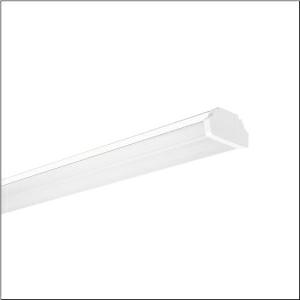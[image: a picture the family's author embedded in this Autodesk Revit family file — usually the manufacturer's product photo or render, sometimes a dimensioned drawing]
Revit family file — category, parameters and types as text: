
# Revit family: dus_31_gen_2_53bd812dv4a5c23sl3_ab9d
name_source: partatom
category: Lighting Fixtures
units: mm (PartAtom-declared; Revit-internal decimal feet)

## family parameters
Cut with Voids When Loaded = No
Host = Face
Light Source = No
Part Type = Normal
Room Calculation Point = No
Round Connector Dimension = Use Diameter
Shared = No

## types (1)
- --- (1 x LED, 950 lm, 6.3 W, 4000K)
    Apparent Load = 6 VA
    CIE Flux Codes = 47 80 95 93 100
    Color Rendering = 80
    Color Temperature = 4000K
    Default Elevation = 1800 mm
    Description = DUS 31 Gen.2, luminaire insert, of sheet steel, coil coated, white, length: 1.535mm, width: 81mm, height: 90mm, 5x system unit, system units: 307mm, LED rated luminous flux: 10.860lm, light colour: 840, SDCM (Standard Deviation of Colour Matching)MacAdam ≤ 3 SDCM (initial), control gear: DALI 2, with plug, 6-pole, with phase selection (L1, L2), mains connection: 220..240V, AC, 50/60Hz, rated input power: 65W, for emergency light function, charging phase on L3 (wire number 3), through-wiring accessed according to module size, converter,control gear: single battery element, battery: LiFePO4, 9Ah, primary optical cover: cover, of PMMA, light emission: direct distribution, primary light characteristic: symmetric, protection rating (complete): IP20, protection rating (LED compartment): IP50, insulation class (complete): insulation class I (protective earthing), certification: CE, UKCA, impact resistance: IK03, permissible ambient temperature for indoor applications: +5..+35°C, standard: EN 60598-2-22, corresponds to IFS (International Featured Standards) requirements for safety and quality in the food industry, reducing of maximum allowable ambient temperature of 5°C with ceiling mounting, packaging unit: 1 piece
    Height = 95 mm
    Lamp = 1 x LED
    Lamp Light Flux = 950 lm
    Lamp Power = 6.3 W
    Lamp count = 1
    Length = 1535 mm
    Luminous efficacy = 151 lm/W
    Manufacturer = Siteco
    ModVariant = No
    Model = 53BD812DV4A5C23SL3
    Mounting Place = Ceiling
    Mounting Type = Pendant
    Number of Poles = 1
    OnlyDefault = Yes
    Power Factor = 1
    Product Name = DUS 31 Gen.2
    Product group = luminaire insert | ceiling pendant
    ProductGroupID = 901
    Protection Class = Protection class I
    Protection Degree = IP 20
    RLX_Detail_Level = 1
    RLX_Emergency_Light_Flux = 0 lm
    RLX_Emergency_Type = 0
    RLX_Emergency_Type_DB = No
    RlxData = <blob elided: 32277 chars, md5=c0ea2925>
    Socket = socket
    Standby Power = 0 W
    System Light Flux = 950 lm
    System Power = 6 W
    Type Comments = : emergency light operation: 3 h
    Type Image = l_1319596.jpg
    URL = http://relux.com
    VarID = @adj_038611
    Voltage = 0 V
    Weight = 0.00 kg
    Width = 81 mm

## geometry (parser evidence)
native form markers: Blend x4, Sweep x12
no freeform markers — native parametric forms only
